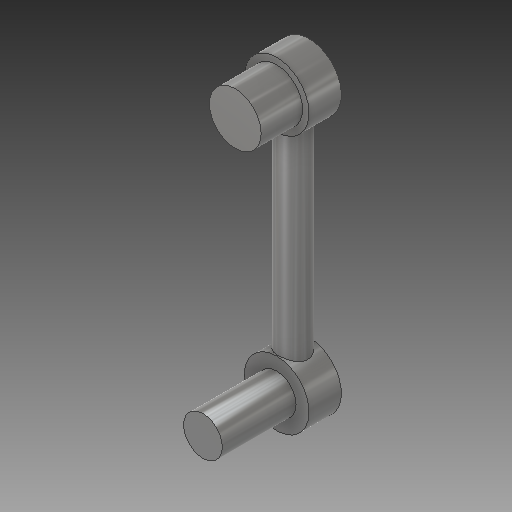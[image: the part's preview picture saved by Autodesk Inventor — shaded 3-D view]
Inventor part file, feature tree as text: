
AUTODESK INVENTOR PART (.ipt)
format: ipt  version: 2019 (Build 230136000, 136)  size: 166,400 bytes
history: native  units: mm
features: sketch x7, extrude x5, revolve x2, projected_geometry x1
ambient origin geometry x8: Origin, YZ Plane, XZ Plane, XY Plane, X Axis, Y Axis, Z Axis, Center Point
bodies: Solid1 (feature_tree)
feature tree (15):
  extrude  "Extrusion1"  Depth=16.0mm TaperAngle=0.0deg
  revolve  "Revolution1"  [1 undecoded]
  extrude  "Extrusion2"  TaperAngle=90.0deg  [1 undecoded]
  extrude  "Extrusion3"  Depth=3.2mm TaperAngle=0.0deg
  revolve  "Revolution2"  [1 undecoded]
  extrude  "Extrusion4"  Depth=2.5mm
  extrude  "Extrusion5"  Depth=0.5mm
  sketch  "Sketch1"  dims[d0=2.3mm d1=16.0mm d2=0.0mm]
  sketch  "Sketch2"  dims[d3=0.5mm d4=1.25mm]
  sketch  "Sketch3"  dims[d7=2.5mm d8=90.0deg]
  sketch  "Sketch4"  dims[d9=4.0mm d10=3.2mm d11=0.0mm]
  sketch  "Sketch5"  dims[d12=1.6mm d13=0.0mm d14=0.5mm]
  sketch  "Sketch6"  dims[d15=1.25mm d16=2.5mm]
  projected_geometry  "Projected Loop1"
  sketch  "Sketch7"  dims[d17=90.0deg d18=3.0mm d19=5.7mm d20=0.0mm d21=0.5mm d22=0.0mm]
note: 3 required parameter values undecoded (feature->parameter linkage not recoverable at this tier; creation-order binding heuristic only, values carry confidence <= 0.55)